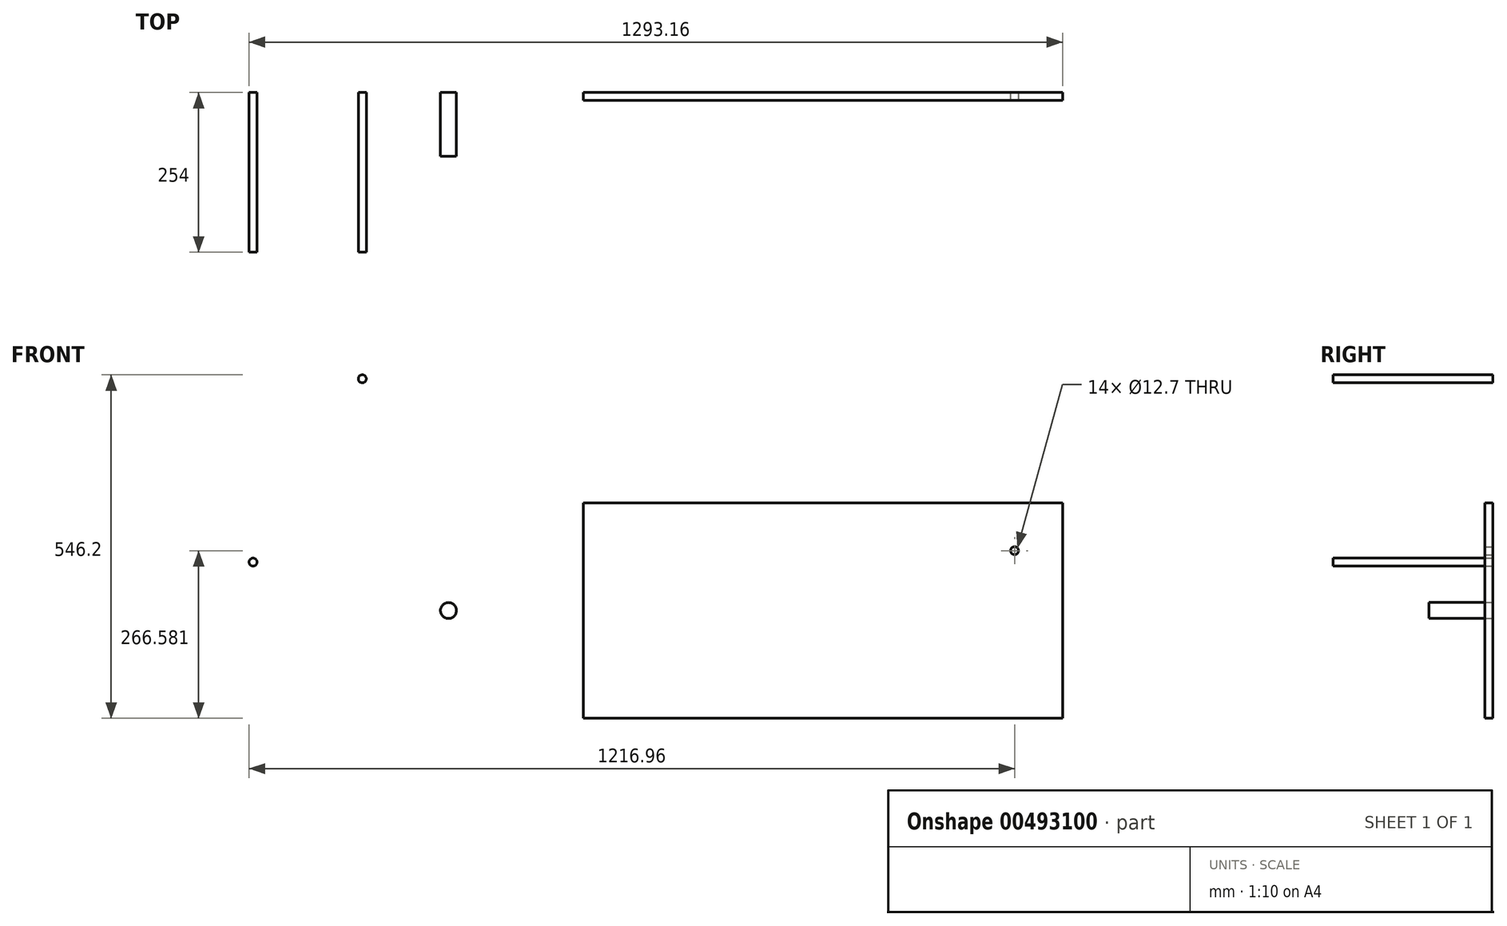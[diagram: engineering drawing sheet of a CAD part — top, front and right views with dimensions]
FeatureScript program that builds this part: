
annotation { "Feature Type Name" : "Feature", "Feature Type Description" : "" }
export const myFeature = defineFeature(function(context is Context, id is Id, definition is map)
    precondition{}
    {
        {
            var Q0;
            Q0=qCreatedBy(makeId("Front.planeOp"),FACE);
            var sketch = newSketch(context, id + "F0", { "sketchPlane" : qUnion([Q0])});
            skLineSegment(sketch, "E0.bottom", {"start": v(124.53, 171.4) * mm, "end": v(-637.47, 171.4) * mm});
            skLineSegment(sketch, "E0.top", {"start": v(124.53, -171.4) * mm, "end": v(-637.47, -171.4) * mm});
            skLineSegment(sketch, "E0.left", {"start": v(124.53, 171.4) * mm, "end": v(124.53, -171.4) * mm});
            skLineSegment(sketch, "E0.right", {"start": v(-637.47, 171.4) * mm, "end": v(-637.47, -171.4) * mm});
            skPoint(sketch, "E0.middle", {"position": v(-256.47, 0) * mm});
            skCircle(sketch, "E1", {"center": v(48.33, 95.2) * mm, "radius": 6.35 * mm});
            skCircle(sketch, "E2", {"center": v(-988.67, 368.46) * mm, "radius": 6.35 * mm});
            skCircle(sketch, "E3", {"center": v(-1162.28, 76.96) * mm, "radius": 6.35 * mm});
            skCircle(sketch, "E4", {"center": v(-1563.9, 194.6) * mm, "radius": 63.5 * mm});
            skCircle(sketch, "E5", {"center": v(30121.93, 882.3) * mm, "radius": 10485.53 * mm});
            skSolve(sketch);
        }
        {
            var Q0;
            Q0=makeQuery(id+"F0.imprint","IMPRINT",FACE,{"disambiguationData":[TD([[makeQuery(id+"F0.imprint","IMPRINT",EDGE,{"derivedFrom":sQuery(id+"F0.wireOp",EDGE,"E0.bottom")}),1.0]])]});
            extrude(context, id + "F1", {"entities" : qUnion([Q0]), "depth" : 12.7 * mm});
        }
        {
            var Q0;
            Q0=qCreatedBy(makeId("Front.planeOp"),FACE);
            var sketch = newSketch(context, id + "F2", { "sketchPlane" : qUnion([Q0])});
            skLineSegment(sketch, "E6.0", {"start": v(-631.12, -165.04) * mm, "end": v(118.18, -165.04) * mm});
            skLineSegment(sketch, "E6.1", {"start": v(-631.12, 165.04) * mm, "end": v(-631.12, -165.04) * mm});
            skLineSegment(sketch, "E6.2", {"start": v(118.18, 165.04) * mm, "end": v(-631.12, 165.04) * mm});
            skLineSegment(sketch, "E6.3", {"start": v(118.18, -165.04) * mm, "end": v(118.18, 165.04) * mm});
            skCircle(sketch, "E7", {"center": v(-746.19, 0) * mm, "radius": 12.7 * mm});
            skCircle(sketch, "E8", {"center": v(-851.62, 0) * mm, "radius": 12.7 * mm});
            skCircle(sketch, "E9", {"center": v(-808.16, 30.44) * mm, "radius": 6.35 * mm});
            skSolve(sketch);
        }
        {
            var Q0;
            Q0=makeQuery(id+"F2.imprint","IMPRINT",FACE,{"disambiguationData":[TD([[makeQuery(id+"F2.imprint","IMPRINT",EDGE,{"derivedFrom":sQuery(id+"F2.wireOp",EDGE,"E8")}),1.0]])]});
            extrude(context, id + "F3", {"entities" : qUnion([Q0]), "depth" : 101.6 * mm});
        }
        {
            var Q0;
            Q0=makeQuery(id+"F0.imprint","IMPRINT",FACE,{"disambiguationData":[TD([[makeQuery(id+"F0.imprint","IMPRINT",EDGE,{"derivedFrom":sQuery(id+"F0.wireOp",EDGE,"E2")}),1.0]])]});
            var Q1;
            Q1=makeQuery(id+"F0.imprint","IMPRINT",FACE,{"disambiguationData":[TD([[makeQuery(id+"F0.imprint","IMPRINT",EDGE,{"derivedFrom":sQuery(id+"F0.wireOp",EDGE,"E3")}),1.0]])]});
            extrude(context, id + "F4", {"entities" : qUnion([Q0, Q1]), "depth" : 254 * mm});
        }
        {
            var Q0;
            Q0=sQuery(id+"F0.wireOp",EDGE,"E4");
            extrude(context, id + "F5", {"bodyType" : ToolBodyType.SURFACE, "surfaceEntities" : qUnion([Q0]), "depth" : 25.4 * mm});
        }
    });
